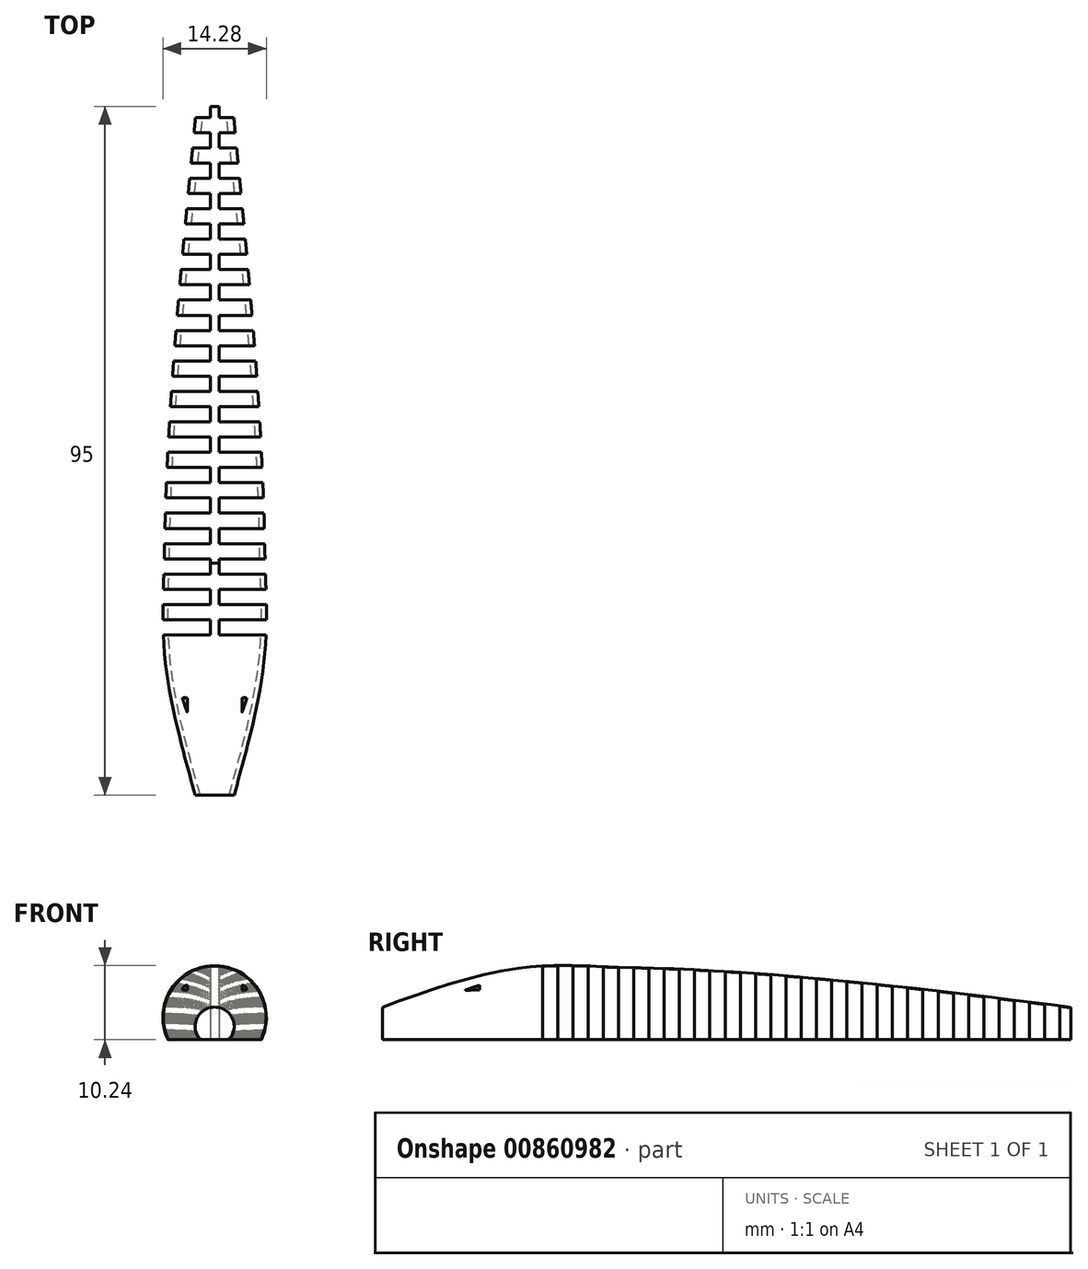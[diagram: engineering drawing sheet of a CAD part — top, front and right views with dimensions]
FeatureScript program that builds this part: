
annotation { "Feature Type Name" : "Feature", "Feature Type Description" : "" }
export const myFeature = defineFeature(function(context is Context, id is Id, definition is map)
    precondition{}
    {
        {
            var Q0;
            Q0=qCreatedBy(makeId("Front.planeOp"),FACE);
            var sketch = newSketch(context, id + "F0", { "sketchPlane" : qUnion([Q0])});
            skArc(sketch, "E0", {"start": v(6.25, 0) * mm, "mid": v(0, 10) * mm, "end": v(-6.25, 0) * mm});
            skPoint(sketch, "E0.first.point", {"position": v(-6.25, 0) * mm});
            skPoint(sketch, "E0.second.point", {"position": v(6.25, 0) * mm});
            skPoint(sketch, "E0.third.point", {"position": v(0, 10) * mm});
            skLineSegment(sketch, "E1", {"start": v(-6.25, 0) * mm, "end": v(6.25, 0) * mm});
            skSolve(sketch);
        }
        {
            var Q0;
            Q0=qCreatedBy(makeId("Front.planeOp"),FACE);
            cPlane(context, id + "F1", {"entities" : qUnion([Q0]), "cplaneType" : CPlaneType.OFFSET, "offset" : 12 * mm, "oppositeDirection" : true, "width" : 150 * mm, "height" : 150 * mm});
        }
        {
            var Q0;
            Q0=qCreatedBy(id+"F1.planeOp",FACE);
            var sketch = newSketch(context, id + "F2", { "sketchPlane" : qUnion([Q0])});
            skArc(sketch, "E2", {"start": v(6.25, 0) * mm, "mid": v(0, 10) * mm, "end": v(-6.25, 0) * mm});
            skPoint(sketch, "E2.first.point", {"position": v(-6.25, 0) * mm});
            skPoint(sketch, "E2.second.point", {"position": v(6.25, 0) * mm});
            skPoint(sketch, "E2.third.point", {"position": v(0, 10) * mm});
            skLineSegment(sketch, "E3", {"start": v(-6.25, 0) * mm, "end": v(6.25, 0) * mm});
            skSolve(sketch);
        }
        {
            var Q0;
            Q0=qCreatedBy(id+"F1.planeOp",FACE);
            cPlane(context, id + "F3", {"entities" : qUnion([Q0]), "cplaneType" : CPlaneType.OFFSET, "offset" : 63 * mm, "oppositeDirection" : true, "width" : 150 * mm, "height" : 150 * mm});
        }
        {
            var Q0;
            Q0=qCreatedBy(id+"F3.planeOp",FACE);
            var sketch = newSketch(context, id + "F4", { "sketchPlane" : qUnion([Q0])});
            skArc(sketch, "E4", {"start": v(1.5, 0) * mm, "mid": v(0, 4.5) * mm, "end": v(-1.5, 0) * mm});
            skPoint(sketch, "E4.first.point", {"position": v(1.5, 0) * mm});
            skPoint(sketch, "E4.second.point", {"position": v(-1.5, 0) * mm});
            skPoint(sketch, "E4.third.point", {"position": v(0, 4.5) * mm});
            skLineSegment(sketch, "E5", {"start": v(1.5, 0) * mm, "end": v(-1.5, 0) * mm});
            skSolve(sketch);
        }
        {
            var Q0;
            Q0=qCreatedBy(makeId("Front.planeOp"),FACE);
            cPlane(context, id + "F5", {"entities" : qUnion([Q0]), "cplaneType" : CPlaneType.OFFSET, "offset" : 20 * mm, "width" : 150 * mm, "height" : 150 * mm});
        }
        {
            var Q0;
            Q0=qCreatedBy(id+"F5.planeOp",FACE);
            var sketch = newSketch(context, id + "F6", { "sketchPlane" : qUnion([Q0])});
            skArc(sketch, "E6", {"start": v(2, 0) * mm, "mid": v(0, 4.5) * mm, "end": v(-2, 0) * mm});
            skPoint(sketch, "E6.first.point", {"position": v(-2, 0) * mm});
            skPoint(sketch, "E6.second.point", {"position": v(2, 0) * mm});
            skPoint(sketch, "E6.third.point", {"position": v(0, 4.5) * mm});
            skLineSegment(sketch, "E7", {"start": v(0, 0) * mm, "end": v(0, 5.46) * mm, "construction": true});
            skLineSegment(sketch, "E8", {"start": v(-2, 0) * mm, "end": v(2, 0) * mm});
            skSolve(sketch);
        }
        {
            var Q0;
            Q0=makeQuery(id+"F6.imprint","IMPRINT",FACE,{"disambiguationData":[TD([[makeQuery(id+"F6.imprint","IMPRINT",EDGE,{"derivedFrom":sQuery(id+"F6.wireOp",EDGE,"E6")}),1.0]])]});
            var Q1;
            Q1=makeQuery(id+"F0.imprint","IMPRINT",FACE,{"disambiguationData":[TD([[makeQuery(id+"F0.imprint","IMPRINT",EDGE,{"derivedFrom":sQuery(id+"F0.wireOp",EDGE,"E0")}),1.0]])]});
            var Q2;
            Q2=makeQuery(id+"F2.imprint","IMPRINT",FACE,{"disambiguationData":[TD([[makeQuery(id+"F2.imprint","IMPRINT",EDGE,{"derivedFrom":sQuery(id+"F2.wireOp",EDGE,"E2")}),1.0]])]});
            loft(context, id + "F7", {"sheetProfilesArray" : [{ "sheetProfileEntities" : qUnion([Q0]) }, { "sheetProfileEntities" : qUnion([Q1]) }, { "sheetProfileEntities" : qUnion([Q2]) }]});
        }
        {
            var Q1;
            Q1 = qSketchRegion(id + "F0", true);
            var Q2;
            Q2 = qSketchRegion(id + "F2", true);
            var Q3;
            Q3 = qSketchRegion(id + "F4", true);
            loft(context, id + "F8", {"operationType" : NewBodyOperationType.ADD, "sheetProfilesArray" : [{ "sheetProfileEntities" : qUnion([Q1]) }, { "sheetProfileEntities" : qUnion([Q2]) }, { "sheetProfileEntities" : qUnion([Q3]) }]});
        }
        {
            var Q0;
            Q0=qCreatedBy(makeId("Top.planeOp"),FACE);
            var sketch = newSketch(context, id + "F9", { "sketchPlane" : qUnion([Q0])});
            skLineSegment(sketch, "E9.bottom", {"start": v(-0.6, 2.1) * mm, "end": v(-9.6, 2.1) * mm});
            skLineSegment(sketch, "E9.top", {"start": v(-0.6, 4.2) * mm, "end": v(-9.6, 4.2) * mm});
            skLineSegment(sketch, "E9.left", {"start": v(-0.6, 2.1) * mm, "end": v(-0.6, 4.2) * mm});
            skLineSegment(sketch, "E9.right", {"start": v(-9.6, 2.1) * mm, "end": v(-9.6, 4.2) * mm});
            skLineSegment(sketch, "E10", {"start": v(0, -33.35) * mm, "end": v(0, 97.2) * mm, "construction": true});
            skLineSegment(sketch, "E11.0.1.0", {"start": v(-0.6, 6.3) * mm, "end": v(-0.6, 8.4) * mm});
            skLineSegment(sketch, "E11.0.1.1", {"start": v(-0.6, 6.3) * mm, "end": v(-9.6, 6.3) * mm});
            skLineSegment(sketch, "E11.0.1.2", {"start": v(-0.6, 8.4) * mm, "end": v(-9.6, 8.4) * mm});
            skLineSegment(sketch, "E11.0.1.3", {"start": v(-9.6, 6.3) * mm, "end": v(-9.6, 8.4) * mm});
            skLineSegment(sketch, "E11.0.2.0", {"start": v(-0.6, 10.5) * mm, "end": v(-0.6, 12.6) * mm});
            skLineSegment(sketch, "E11.0.2.1", {"start": v(-0.6, 10.5) * mm, "end": v(-9.6, 10.5) * mm});
            skLineSegment(sketch, "E11.0.2.2", {"start": v(-0.6, 12.6) * mm, "end": v(-9.6, 12.6) * mm});
            skLineSegment(sketch, "E11.0.2.3", {"start": v(-9.6, 10.5) * mm, "end": v(-9.6, 12.6) * mm});
            skLineSegment(sketch, "E11.0.3.0", {"start": v(-0.6, 14.7) * mm, "end": v(-0.6, 16.8) * mm});
            skLineSegment(sketch, "E11.0.3.1", {"start": v(-0.6, 14.7) * mm, "end": v(-9.6, 14.7) * mm});
            skLineSegment(sketch, "E11.0.3.2", {"start": v(-0.6, 16.8) * mm, "end": v(-9.6, 16.8) * mm});
            skLineSegment(sketch, "E11.0.3.3", {"start": v(-9.6, 14.7) * mm, "end": v(-9.6, 16.8) * mm});
            skLineSegment(sketch, "E11.0.4.0", {"start": v(-0.6, 18.9) * mm, "end": v(-0.6, 21) * mm});
            skLineSegment(sketch, "E11.0.4.1", {"start": v(-0.6, 18.9) * mm, "end": v(-9.6, 18.9) * mm});
            skLineSegment(sketch, "E11.0.4.2", {"start": v(-0.6, 21) * mm, "end": v(-9.6, 21) * mm});
            skLineSegment(sketch, "E11.0.4.3", {"start": v(-9.6, 18.9) * mm, "end": v(-9.6, 21) * mm});
            skLineSegment(sketch, "E11.0.5.0", {"start": v(-0.6, 23.1) * mm, "end": v(-0.6, 25.2) * mm});
            skLineSegment(sketch, "E11.0.5.1", {"start": v(-0.6, 23.1) * mm, "end": v(-9.6, 23.1) * mm});
            skLineSegment(sketch, "E11.0.5.2", {"start": v(-0.6, 25.2) * mm, "end": v(-9.6, 25.2) * mm});
            skLineSegment(sketch, "E11.0.5.3", {"start": v(-9.6, 23.1) * mm, "end": v(-9.6, 25.2) * mm});
            skLineSegment(sketch, "E11.0.6.0", {"start": v(-0.6, 27.3) * mm, "end": v(-0.6, 29.4) * mm});
            skLineSegment(sketch, "E11.0.6.1", {"start": v(-0.6, 27.3) * mm, "end": v(-9.6, 27.3) * mm});
            skLineSegment(sketch, "E11.0.6.2", {"start": v(-0.6, 29.4) * mm, "end": v(-9.6, 29.4) * mm});
            skLineSegment(sketch, "E11.0.6.3", {"start": v(-9.6, 27.3) * mm, "end": v(-9.6, 29.4) * mm});
            skLineSegment(sketch, "E11.0.7.0", {"start": v(-0.6, 31.5) * mm, "end": v(-0.6, 33.6) * mm});
            skLineSegment(sketch, "E11.0.7.1", {"start": v(-0.6, 31.5) * mm, "end": v(-9.6, 31.5) * mm});
            skLineSegment(sketch, "E11.0.7.2", {"start": v(-0.6, 33.6) * mm, "end": v(-9.6, 33.6) * mm});
            skLineSegment(sketch, "E11.0.7.3", {"start": v(-9.6, 31.5) * mm, "end": v(-9.6, 33.6) * mm});
            skLineSegment(sketch, "E11.0.8.0", {"start": v(-0.6, 35.7) * mm, "end": v(-0.6, 37.8) * mm});
            skLineSegment(sketch, "E11.0.8.1", {"start": v(-0.6, 35.7) * mm, "end": v(-9.6, 35.7) * mm});
            skLineSegment(sketch, "E11.0.8.2", {"start": v(-0.6, 37.8) * mm, "end": v(-9.6, 37.8) * mm});
            skLineSegment(sketch, "E11.0.8.3", {"start": v(-9.6, 35.7) * mm, "end": v(-9.6, 37.8) * mm});
            skLineSegment(sketch, "E11.0.9.0", {"start": v(-0.6, 39.9) * mm, "end": v(-0.6, 42) * mm});
            skLineSegment(sketch, "E11.0.9.1", {"start": v(-0.6, 39.9) * mm, "end": v(-9.6, 39.9) * mm});
            skLineSegment(sketch, "E11.0.9.2", {"start": v(-0.6, 42) * mm, "end": v(-9.6, 42) * mm});
            skLineSegment(sketch, "E11.0.9.3", {"start": v(-9.6, 39.9) * mm, "end": v(-9.6, 42) * mm});
            skLineSegment(sketch, "E11.0.10.0", {"start": v(-0.6, 44.1) * mm, "end": v(-0.6, 46.2) * mm});
            skLineSegment(sketch, "E11.0.10.1", {"start": v(-0.6, 44.1) * mm, "end": v(-9.6, 44.1) * mm});
            skLineSegment(sketch, "E11.0.10.2", {"start": v(-0.6, 46.2) * mm, "end": v(-9.6, 46.2) * mm});
            skLineSegment(sketch, "E11.0.10.3", {"start": v(-9.6, 44.1) * mm, "end": v(-9.6, 46.2) * mm});
            skLineSegment(sketch, "E11.0.11.0", {"start": v(-0.6, 48.3) * mm, "end": v(-0.6, 50.4) * mm});
            skLineSegment(sketch, "E11.0.11.1", {"start": v(-0.6, 48.3) * mm, "end": v(-9.6, 48.3) * mm});
            skLineSegment(sketch, "E11.0.11.2", {"start": v(-0.6, 50.4) * mm, "end": v(-9.6, 50.4) * mm});
            skLineSegment(sketch, "E11.0.11.3", {"start": v(-9.6, 48.3) * mm, "end": v(-9.6, 50.4) * mm});
            skLineSegment(sketch, "E11.0.12.0", {"start": v(-0.6, 52.5) * mm, "end": v(-0.6, 54.6) * mm});
            skLineSegment(sketch, "E11.0.12.1", {"start": v(-0.6, 52.5) * mm, "end": v(-9.6, 52.5) * mm});
            skLineSegment(sketch, "E11.0.12.2", {"start": v(-0.6, 54.6) * mm, "end": v(-9.6, 54.6) * mm});
            skLineSegment(sketch, "E11.0.12.3", {"start": v(-9.6, 52.5) * mm, "end": v(-9.6, 54.6) * mm});
            skLineSegment(sketch, "E11.0.13.0", {"start": v(-0.6, 56.7) * mm, "end": v(-0.6, 58.8) * mm});
            skLineSegment(sketch, "E11.0.13.1", {"start": v(-0.6, 56.7) * mm, "end": v(-9.6, 56.7) * mm});
            skLineSegment(sketch, "E11.0.13.2", {"start": v(-0.6, 58.8) * mm, "end": v(-9.6, 58.8) * mm});
            skLineSegment(sketch, "E11.0.13.3", {"start": v(-9.6, 56.7) * mm, "end": v(-9.6, 58.8) * mm});
            skLineSegment(sketch, "E11.0.14.0", {"start": v(-0.6, 60.9) * mm, "end": v(-0.6, 63) * mm});
            skLineSegment(sketch, "E11.0.14.1", {"start": v(-0.6, 60.9) * mm, "end": v(-9.6, 60.9) * mm});
            skLineSegment(sketch, "E11.0.14.2", {"start": v(-0.6, 63) * mm, "end": v(-9.6, 63) * mm});
            skLineSegment(sketch, "E11.0.14.3", {"start": v(-9.6, 60.9) * mm, "end": v(-9.6, 63) * mm});
            skLineSegment(sketch, "E11.0.15.0", {"start": v(-0.6, 65.1) * mm, "end": v(-0.6, 67.2) * mm});
            skLineSegment(sketch, "E11.0.15.1", {"start": v(-0.6, 65.1) * mm, "end": v(-9.6, 65.1) * mm});
            skLineSegment(sketch, "E11.0.15.2", {"start": v(-0.6, 67.2) * mm, "end": v(-9.6, 67.2) * mm});
            skLineSegment(sketch, "E11.0.15.3", {"start": v(-9.6, 65.1) * mm, "end": v(-9.6, 67.2) * mm});
            skLineSegment(sketch, "E11.0.16.0", {"start": v(-0.6, 69.3) * mm, "end": v(-0.6, 71.4) * mm});
            skLineSegment(sketch, "E11.0.16.1", {"start": v(-0.6, 69.3) * mm, "end": v(-9.6, 69.3) * mm});
            skLineSegment(sketch, "E11.0.16.2", {"start": v(-0.6, 71.4) * mm, "end": v(-9.6, 71.4) * mm});
            skLineSegment(sketch, "E11.0.16.3", {"start": v(-9.6, 69.3) * mm, "end": v(-9.6, 71.4) * mm});
            skLineSegment(sketch, "E11.0.17.0", {"start": v(-0.6, 73.5) * mm, "end": v(-0.6, 75.6) * mm});
            skLineSegment(sketch, "E11.0.17.1", {"start": v(-0.6, 73.5) * mm, "end": v(-9.6, 73.5) * mm});
            skLineSegment(sketch, "E11.0.17.2", {"start": v(-0.6, 75.6) * mm, "end": v(-9.6, 75.6) * mm});
            skLineSegment(sketch, "E11.0.17.3", {"start": v(-9.6, 73.5) * mm, "end": v(-9.6, 75.6) * mm});
            skLineSegment(sketch, "E11.direction1", {"start": v(-9.6, 2.1) * mm, "end": v(15.4, 2.1) * mm, "construction": true});
            skLineSegment(sketch, "E11.direction2", {"start": v(-9.6, 2.1) * mm, "end": v(-9.6, 6.3) * mm, "construction": true});
            skLineSegment(sketch, "E12.MirrorCS", {"start": v(0.6, 60.9) * mm, "end": v(9.6, 60.9) * mm});
            skLineSegment(sketch, "E13.MirrorCS", {"start": v(0.6, 25.2) * mm, "end": v(9.6, 25.2) * mm});
            skLineSegment(sketch, "E14.MirrorCS", {"start": v(0.6, 56.7) * mm, "end": v(9.6, 56.7) * mm});
            skLineSegment(sketch, "E15.MirrorCS", {"start": v(9.6, 2.1) * mm, "end": v(9.6, 6.3) * mm, "construction": true});
            skLineSegment(sketch, "E16.MirrorCS", {"start": v(0.6, 21) * mm, "end": v(9.6, 21) * mm});
            skLineSegment(sketch, "E17.MirrorCS", {"start": v(0.6, 42) * mm, "end": v(9.6, 42) * mm});
            skLineSegment(sketch, "E18.MirrorCS", {"start": v(0.6, 10.5) * mm, "end": v(9.6, 10.5) * mm});
            skLineSegment(sketch, "E19.MirrorCS", {"start": v(0.6, 73.5) * mm, "end": v(9.6, 73.5) * mm});
            skLineSegment(sketch, "E20.MirrorCS", {"start": v(0.6, 4.2) * mm, "end": v(9.6, 4.2) * mm});
            skLineSegment(sketch, "E21.MirrorCS", {"start": v(0.6, 37.8) * mm, "end": v(9.6, 37.8) * mm});
            skLineSegment(sketch, "E22.MirrorCS", {"start": v(0.6, 58.8) * mm, "end": v(9.6, 58.8) * mm});
            skLineSegment(sketch, "E23.MirrorCS", {"start": v(0.6, 54.6) * mm, "end": v(9.6, 54.6) * mm});
            skLineSegment(sketch, "E24.MirrorCS", {"start": v(0.6, 75.6) * mm, "end": v(9.6, 75.6) * mm});
            skLineSegment(sketch, "E25.MirrorCS", {"start": v(9.6, 27.3) * mm, "end": v(9.6, 29.4) * mm});
            skLineSegment(sketch, "E26.MirrorCS", {"start": v(0.6, 12.6) * mm, "end": v(9.6, 12.6) * mm});
            skLineSegment(sketch, "E27.MirrorCS", {"start": v(9.6, 14.7) * mm, "end": v(9.6, 16.8) * mm});
            skLineSegment(sketch, "E28.MirrorCS", {"start": v(0.6, 2.1) * mm, "end": v(0.6, 4.2) * mm});
            skLineSegment(sketch, "E29.MirrorCS", {"start": v(0.6, 71.4) * mm, "end": v(9.6, 71.4) * mm});
            skLineSegment(sketch, "E30.MirrorCS", {"start": v(9.6, 44.1) * mm, "end": v(9.6, 46.2) * mm});
            skLineSegment(sketch, "E31.MirrorCS", {"start": v(9.6, 31.5) * mm, "end": v(9.6, 33.6) * mm});
            skLineSegment(sketch, "E32.MirrorCS", {"start": v(0.6, 31.5) * mm, "end": v(0.6, 33.6) * mm});
            skLineSegment(sketch, "E33.MirrorCS", {"start": v(9.6, 60.9) * mm, "end": v(9.6, 63) * mm});
            skLineSegment(sketch, "E34.MirrorCS", {"start": v(9.6, 48.3) * mm, "end": v(9.6, 50.4) * mm});
            skLineSegment(sketch, "E35.MirrorCS", {"start": v(9.6, 10.5) * mm, "end": v(9.6, 12.6) * mm});
            skLineSegment(sketch, "E36.MirrorCS", {"start": v(0.6, 27.3) * mm, "end": v(0.6, 29.4) * mm});
            skLineSegment(sketch, "E37.MirrorCS", {"start": v(9.6, 2.1) * mm, "end": v(9.6, 4.2) * mm});
            skLineSegment(sketch, "E38.MirrorCS", {"start": v(0.6, 48.3) * mm, "end": v(0.6, 50.4) * mm});
            skLineSegment(sketch, "E39.MirrorCS", {"start": v(9.6, 65.1) * mm, "end": v(9.6, 67.2) * mm});
            skLineSegment(sketch, "E40.MirrorCS", {"start": v(0.6, 23.1) * mm, "end": v(0.6, 25.2) * mm});
            skLineSegment(sketch, "E41.MirrorCS", {"start": v(0.6, 44.1) * mm, "end": v(0.6, 46.2) * mm});
            skLineSegment(sketch, "E42.MirrorCS", {"start": v(0.6, 65.1) * mm, "end": v(0.6, 67.2) * mm});
            skLineSegment(sketch, "E43.MirrorCS", {"start": v(0.6, 39.9) * mm, "end": v(0.6, 42) * mm});
            skLineSegment(sketch, "E44.MirrorCS", {"start": v(0.6, 60.9) * mm, "end": v(0.6, 63) * mm});
            skLineSegment(sketch, "E45.MirrorCS", {"start": v(0.6, 56.7) * mm, "end": v(0.6, 58.8) * mm});
            skLineSegment(sketch, "E46.MirrorCS", {"start": v(0.6, 18.9) * mm, "end": v(9.6, 18.9) * mm});
            skLineSegment(sketch, "E47.MirrorCS", {"start": v(0.6, 73.5) * mm, "end": v(0.6, 75.6) * mm});
            skLineSegment(sketch, "E48.MirrorCS", {"start": v(0.6, 6.3) * mm, "end": v(0.6, 8.4) * mm});
            skLineSegment(sketch, "E49.MirrorCS", {"start": v(0.6, 35.7) * mm, "end": v(9.6, 35.7) * mm});
            skLineSegment(sketch, "E50.MirrorCS", {"start": v(0.6, 33.6) * mm, "end": v(9.6, 33.6) * mm});
            skLineSegment(sketch, "E51.MirrorCS", {"start": v(0.6, 52.5) * mm, "end": v(9.6, 52.5) * mm});
            skLineSegment(sketch, "E52.MirrorCS", {"start": v(0.6, 29.4) * mm, "end": v(9.6, 29.4) * mm});
            skLineSegment(sketch, "E53.MirrorCS", {"start": v(0.6, 50.4) * mm, "end": v(9.6, 50.4) * mm});
            skLineSegment(sketch, "E54.MirrorCS", {"start": v(0.6, 6.3) * mm, "end": v(9.6, 6.3) * mm});
            skLineSegment(sketch, "E55.MirrorCS", {"start": v(0.6, 69.3) * mm, "end": v(9.6, 69.3) * mm});
            skLineSegment(sketch, "E56.MirrorCS", {"start": v(0.6, 46.2) * mm, "end": v(9.6, 46.2) * mm});
            skLineSegment(sketch, "E57.MirrorCS", {"start": v(0.6, 67.2) * mm, "end": v(9.6, 67.2) * mm});
            skLineSegment(sketch, "E58.MirrorCS", {"start": v(0.6, 14.7) * mm, "end": v(0.6, 16.8) * mm});
            skLineSegment(sketch, "E59.MirrorCS", {"start": v(0.6, 63) * mm, "end": v(9.6, 63) * mm});
            skLineSegment(sketch, "E60.MirrorCS", {"start": v(9.6, 23.1) * mm, "end": v(9.6, 25.2) * mm});
            skLineSegment(sketch, "E61.MirrorCS", {"start": v(9.6, 18.9) * mm, "end": v(9.6, 21) * mm});
            skLineSegment(sketch, "E62.MirrorCS", {"start": v(9.6, 39.9) * mm, "end": v(9.6, 42) * mm});
            skLineSegment(sketch, "E63.MirrorCS", {"start": v(0.6, 14.7) * mm, "end": v(9.6, 14.7) * mm});
            skLineSegment(sketch, "E64.MirrorCS", {"start": v(9.6, 35.7) * mm, "end": v(9.6, 37.8) * mm});
            skLineSegment(sketch, "E65.MirrorCS", {"start": v(9.6, 56.7) * mm, "end": v(9.6, 58.8) * mm});
            skLineSegment(sketch, "E66.MirrorCS", {"start": v(9.6, 52.5) * mm, "end": v(9.6, 54.6) * mm});
            skLineSegment(sketch, "E67.MirrorCS", {"start": v(9.6, 73.5) * mm, "end": v(9.6, 75.6) * mm});
            skLineSegment(sketch, "E68.MirrorCS", {"start": v(0.6, 16.8) * mm, "end": v(9.6, 16.8) * mm});
            skLineSegment(sketch, "E69.MirrorCS", {"start": v(0.6, 8.4) * mm, "end": v(9.6, 8.4) * mm});
            skLineSegment(sketch, "E70.MirrorCS", {"start": v(0.6, 18.9) * mm, "end": v(0.6, 21) * mm});
            skLineSegment(sketch, "E71.MirrorCS", {"start": v(9.6, 69.3) * mm, "end": v(9.6, 71.4) * mm});
            skLineSegment(sketch, "E72.MirrorCS", {"start": v(0.6, 35.7) * mm, "end": v(0.6, 37.8) * mm});
            skLineSegment(sketch, "E73.MirrorCS", {"start": v(0.6, 31.5) * mm, "end": v(9.6, 31.5) * mm});
            skLineSegment(sketch, "E74.MirrorCS", {"start": v(9.6, 6.3) * mm, "end": v(9.6, 8.4) * mm});
            skLineSegment(sketch, "E75.MirrorCS", {"start": v(0.6, 52.5) * mm, "end": v(0.6, 54.6) * mm});
            skLineSegment(sketch, "E76.MirrorCS", {"start": v(0.6, 27.3) * mm, "end": v(9.6, 27.3) * mm});
            skLineSegment(sketch, "E77.MirrorCS", {"start": v(0.6, 48.3) * mm, "end": v(9.6, 48.3) * mm});
            skLineSegment(sketch, "E78.MirrorCS", {"start": v(0.6, 69.3) * mm, "end": v(0.6, 71.4) * mm});
            skLineSegment(sketch, "E79.MirrorCS", {"start": v(0.6, 23.1) * mm, "end": v(9.6, 23.1) * mm});
            skLineSegment(sketch, "E80.MirrorCS", {"start": v(0.6, 44.1) * mm, "end": v(9.6, 44.1) * mm});
            skLineSegment(sketch, "E81.MirrorCS", {"start": v(0.6, 65.1) * mm, "end": v(9.6, 65.1) * mm});
            skLineSegment(sketch, "E82.MirrorCS", {"start": v(0.6, 10.5) * mm, "end": v(0.6, 12.6) * mm});
            skLineSegment(sketch, "E83.MirrorCS", {"start": v(0.6, 39.9) * mm, "end": v(9.6, 39.9) * mm});
            skLineSegment(sketch, "E84.MirrorCS", {"start": v(0.6, 2.1) * mm, "end": v(9.6, 2.1) * mm});
            skSolve(sketch);
        }
        {
            var Q0;
            Q0 = qSketchRegion(id + "F9", true);
            extrude(context, id + "F10", {"entities" : qUnion([Q0]), "operationType" : NewBodyOperationType.REMOVE, "endBound" : BoundingType.THROUGH_ALL, "depth" : 25 * mm, "offsetDistance" : 25 * mm});
        }
        {
            var Q0;
            Q0=qCreatedBy(makeId("Right.planeOp"),FACE);
            cPlane(context, id + "F11", {"entities" : qUnion([Q0]), "cplaneType" : CPlaneType.OFFSET, "offset" : 3.8 * mm, "width" : 150 * mm, "height" : 150 * mm});
        }
        {
            var Q0;
            Q0=qCreatedBy(id+"F11.planeOp",FACE);
            var sketch = newSketch(context, id + "F12", { "sketchPlane" : qUnion([Q0])});
            skFitSpline(sketch, "E85", {"points": [v(12, 8.87) * mm, v(10.17, 8.98) * mm, v(7.43, 9.14) * mm, v(3.76, 9.15) * mm, v(1.48, 9.03) * mm, v(-0.34, 8.84) * mm, v(-2.15, 8.57) * mm, v(-4.38, 8.1) * mm, v(-7, 7.38) * mm, v(-8.73, 6.78) * mm, v(-9.58, 6.46) * mm, v(-10.33, 6.17) * mm, v(-11.44, 5.7) * mm, v(-12.89, 5) * mm, v(-13.59, 4.6) * mm, v(-13.93, 4.4) * mm, v(-14.24, 4.2) * mm, v(-14.7, 3.9) * mm, v(-15.25, 3.42) * mm, v(-15.5, 3.15) * mm, v(-15.6, 3) * mm, v(-15.72, 2.85) * mm, v(-15.87, 2.6) * mm, v(-15.95, 2.21) * mm, v(-15.93, 2.02) * mm, v(-15.9, 1.92) * mm, v(-15.86, 1.72) * mm, v(-15.64, 1.36) * mm, v(-15.33, 1.08) * mm, v(-15.17, 0.96) * mm, v(-14.9, 0.75) * mm, v(-14.32, 0.41) * mm, v(-13.7, 0.13) * mm, v(-13.37, 0) * mm]});
            skFitSpline(sketch, "E86", {"points": [v(12, 8.87) * mm, v(10.17, 8.98) * mm, v(7.43, 9.14) * mm, v(3.76, 9.15) * mm, v(1.48, 9.03) * mm, v(-0.34, 8.84) * mm, v(-2.15, 8.57) * mm, v(-4.38, 8.1) * mm, v(-7, 7.38) * mm, v(-8.73, 6.78) * mm, v(-9.58, 6.46) * mm, v(-10.33, 6.17) * mm, v(-11.44, 5.7) * mm, v(-12.89, 5) * mm, v(-13.59, 4.6) * mm, v(-13.93, 4.4) * mm, v(-14.24, 4.2) * mm, v(-14.7, 3.9) * mm, v(-15.25, 3.42) * mm, v(-15.5, 3.15) * mm, v(-15.6, 3) * mm, v(-15.72, 2.85) * mm, v(-15.87, 2.6) * mm, v(-15.95, 2.21) * mm, v(-15.93, 2.02) * mm, v(-15.9, 1.92) * mm, v(-15.86, 1.72) * mm, v(-15.64, 1.36) * mm, v(-15.33, 1.08) * mm, v(-15.17, 0.96) * mm, v(-14.9, 0.75) * mm, v(-14.32, 0.41) * mm, v(-13.7, 0.13) * mm, v(-13.37, 0) * mm]});
            skFitSpline(sketch, "E87", {"points": [v(12, 8.87) * mm, v(10.17, 8.98) * mm, v(7.43, 9.14) * mm, v(3.76, 9.15) * mm, v(1.48, 9.03) * mm, v(-0.34, 8.84) * mm, v(-2.15, 8.57) * mm, v(-4.38, 8.1) * mm, v(-7, 7.38) * mm, v(-8.73, 6.78) * mm, v(-9.58, 6.46) * mm, v(-10.33, 6.17) * mm, v(-11.44, 5.7) * mm, v(-12.89, 5) * mm, v(-13.59, 4.6) * mm, v(-13.93, 4.4) * mm, v(-14.24, 4.2) * mm, v(-14.7, 3.9) * mm, v(-15.25, 3.42) * mm, v(-15.5, 3.15) * mm, v(-15.6, 3) * mm, v(-15.72, 2.85) * mm, v(-15.87, 2.6) * mm, v(-15.95, 2.21) * mm, v(-15.93, 2.02) * mm, v(-15.9, 1.92) * mm, v(-15.86, 1.72) * mm, v(-15.64, 1.36) * mm, v(-15.33, 1.08) * mm, v(-15.17, 0.96) * mm, v(-14.9, 0.75) * mm, v(-14.32, 0.41) * mm, v(-13.7, 0.13) * mm, v(-13.37, 0) * mm]});
            skArc(sketch, "E88", {"start": v(-6.5, 6.85) * mm, "mid": v(-8.5, 8.85) * mm, "end": v(-10.5, 6.85) * mm});
            skLineSegment(sketch, "E89", {"start": v(-8.5, 6.85) * mm, "end": v(-6.5, 6.85) * mm});
            skLineSegment(sketch, "E90", {"start": v(-8.5, 6.85) * mm, "end": v(-10.5, 6.85) * mm});
            skFitSpline(sketch, "E91.trimOffspring", {"points": [v(12, 8.87) * mm, v(10.17, 8.98) * mm, v(7.43, 9.14) * mm, v(3.76, 9.15) * mm, v(1.48, 9.03) * mm, v(-0.34, 8.84) * mm, v(-2.15, 8.57) * mm, v(-4.38, 8.1) * mm, v(-7, 7.38) * mm, v(-8.73, 6.78) * mm, v(-9.58, 6.46) * mm, v(-10.33, 6.17) * mm, v(-11.44, 5.7) * mm, v(-12.89, 5) * mm, v(-13.59, 4.6) * mm, v(-13.93, 4.4) * mm, v(-14.24, 4.2) * mm, v(-14.7, 3.9) * mm, v(-15.25, 3.42) * mm, v(-15.5, 3.15) * mm, v(-15.6, 3) * mm, v(-15.72, 2.85) * mm, v(-15.87, 2.6) * mm, v(-15.95, 2.21) * mm, v(-15.93, 2.02) * mm, v(-15.9, 1.92) * mm, v(-15.86, 1.72) * mm, v(-15.64, 1.36) * mm, v(-15.33, 1.08) * mm, v(-15.17, 0.96) * mm, v(-14.9, 0.75) * mm, v(-14.32, 0.41) * mm, v(-13.7, 0.13) * mm, v(-13.37, 0) * mm]});
            skSolve(sketch);
        }
        {
            var Q0;
            {var subQ2=sQuery(id+"F12.wireOp",EDGE,"E89");Q0=makeQuery(id+"F12.imprint","IMPRINT",FACE,{"disambiguationData":[TD([[makeQuery(id+"F12.imprint","IMPRINT",EDGE,{"derivedFrom":subQ2}),1.0]])]});}
            var Q1;
            Q1=sQuery(id+"F12.wireOp",EDGE,"E90");
            revolve(context, id + "F13", {"surfaceOperationType" : NewSurfaceOperationType.NEW, "entities" : qUnion([Q0]), "axis" : qUnion([Q1]), "revolveType" : RevolveType.FULL});
        }
        {
            var Q0;
            Q0=makeQuery(id+"F13.opRevolve","SWEPT_BODY",BODY,{"disambiguationData":[OSD([sQuery(id+"F12.wireOp",EDGE,"E88"),sQuery(id+"F12.wireOp",EDGE,"E89"),sQuery(id+"F12.wireOp",EDGE,"E90")])]});
            var Q1;
            Q1=qCreatedBy(makeId("Right.planeOp"),FACE);
            mirror(context, id + "F14", {"operationType" : NewBodyOperationType.ADD, "entities" : qUnion([Q0]), "mirrorPlane" : qUnion([Q1])});
        }
    });
